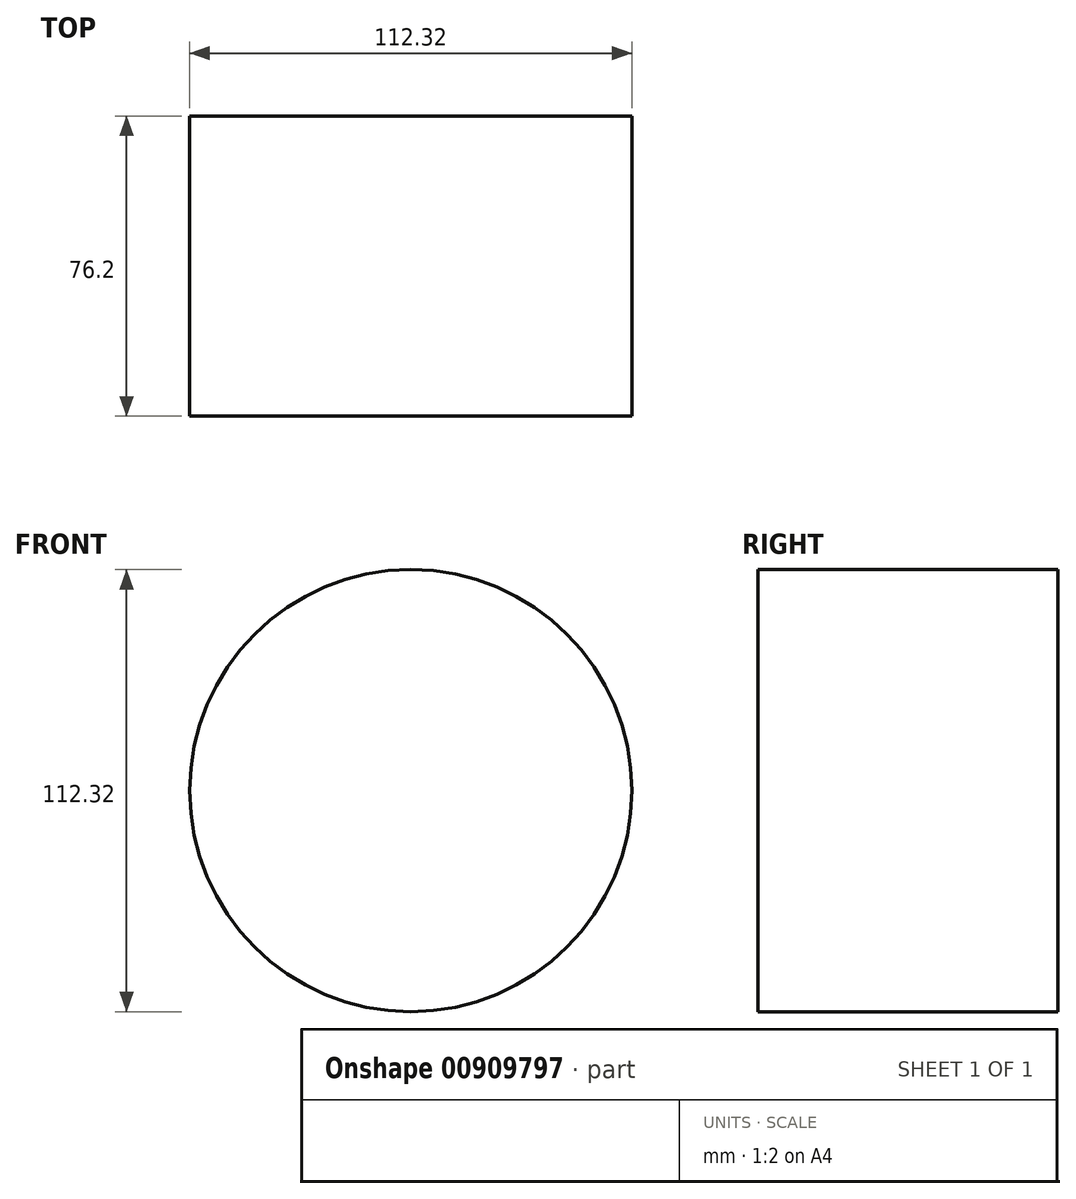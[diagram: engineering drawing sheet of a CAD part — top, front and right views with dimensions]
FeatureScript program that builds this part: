
annotation { "Feature Type Name" : "Feature", "Feature Type Description" : "" }
export const myFeature = defineFeature(function(context is Context, id is Id, definition is map)
    precondition{}
    {
        {
            var Q0;
            Q0=qCreatedBy(makeId("Front.planeOp"),FACE);
            var sketch = newSketch(context, id + "F0", { "sketchPlane" : qUnion([Q0])});
            skCircle(sketch, "E0", {"center": v(0, 0) * mm, "radius": 56.16 * mm});
            skSolve(sketch);
        }
        {
            var Q0;
            Q0 = qSketchRegion(id + "F0", true);
            extrude(context, id + "F1", {"entities" : qUnion([Q0]), "depth" : 76.2 * mm, "offsetDistance" : 25.4 * mm});
        }
    });
